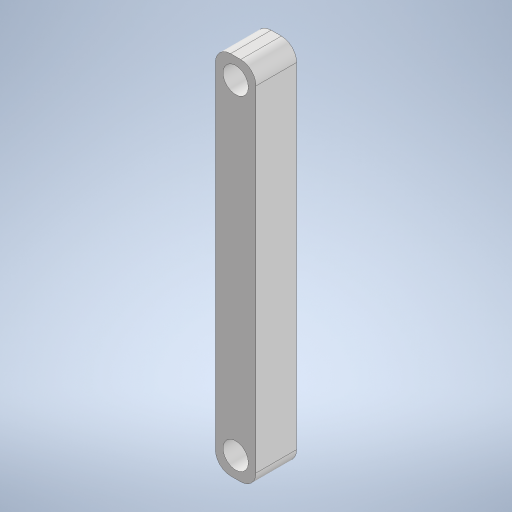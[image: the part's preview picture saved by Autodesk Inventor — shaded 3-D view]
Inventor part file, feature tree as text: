
AUTODESK INVENTOR PART (.ipt)
format: ipt  version: 2024.1 (Build 281209000, 209)  size: 247,296 bytes
history: native  units: mm
features: extrude x1, fillet x1, sketch x1
ambient origin geometry x8: Origin, YZ Plane, XZ Plane, XY Plane, X Axis, Y Axis, Z Axis, Center Point
bodies: Solid1 (feature_tree)
feature tree (3):
  extrude  "Extrusion1"  Depth=72.0mm
  fillet  "Fillet1"  Radius=5.0mm
  sketch  "Sketch1"  dims[d0=8.0mm d1=72.0mm d2=5.0mm d3=5.0mm d4=4.0mm d5=64.0mm d7=4.0mm d8=4.0mm d9=8.0mm d10=0.0mm d11=3.0mm]
